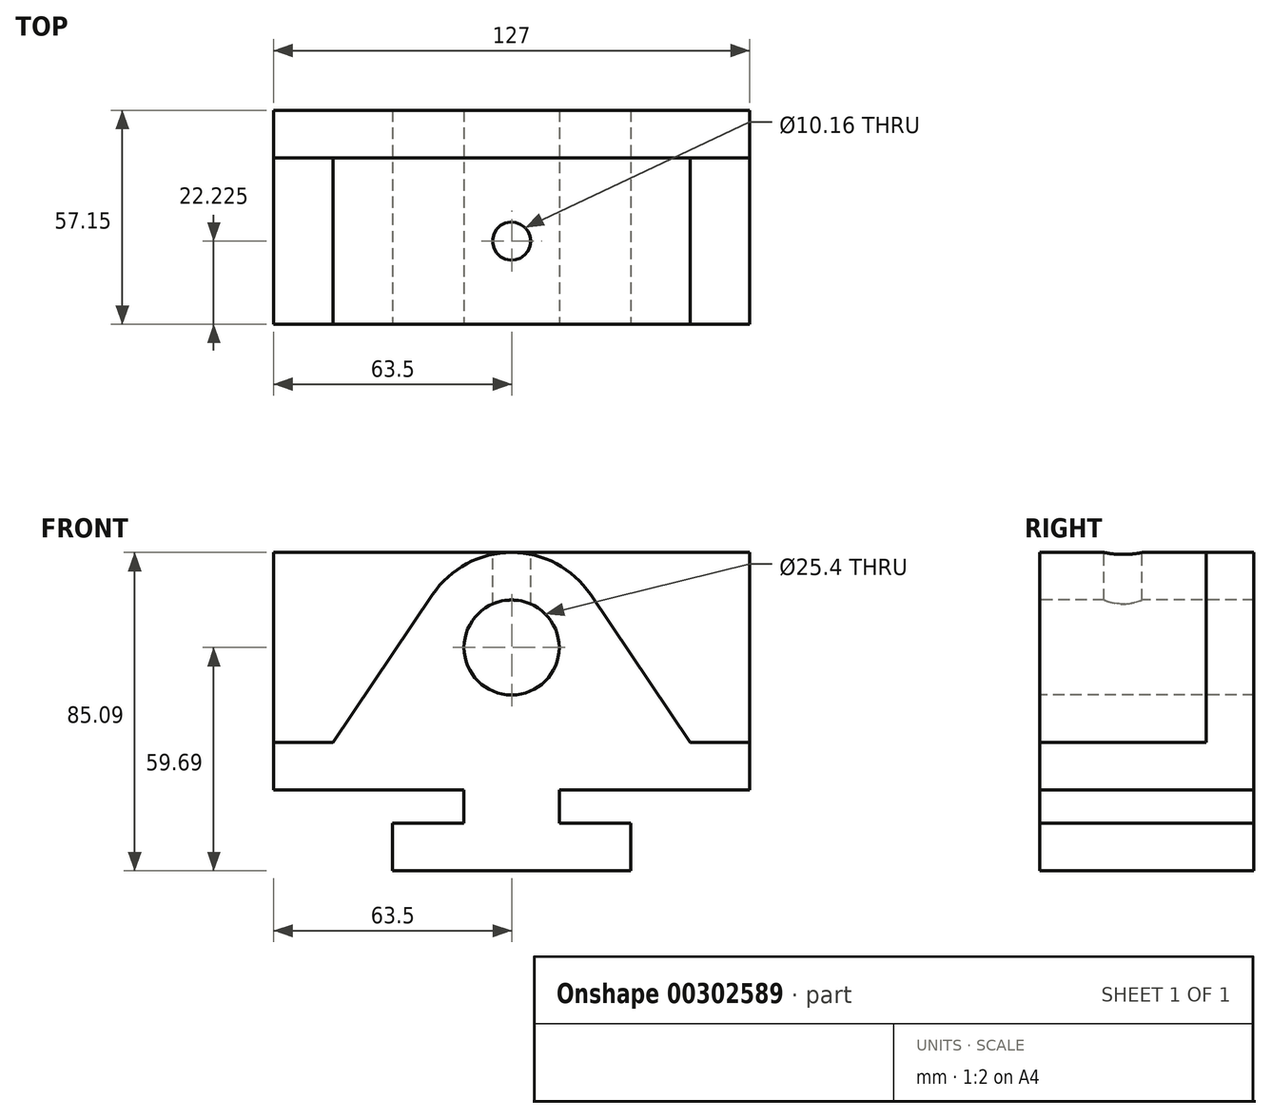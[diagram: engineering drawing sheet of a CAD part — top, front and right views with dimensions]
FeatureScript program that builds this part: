
annotation { "Feature Type Name" : "Feature", "Feature Type Description" : "" }
export const myFeature = defineFeature(function(context is Context, id is Id, definition is map)
    precondition{}
    {
        {
            var Q0;
            Q0=qCreatedBy(makeId("Front.planeOp"),FACE);
            var sketch = newSketch(context, id + "F0", { "sketchPlane" : qUnion([Q0])});
            skLineSegment(sketch, "E0.bottom", {"start": v(0, 0) * mm, "end": v(50.8, 0) * mm});
            skLineSegment(sketch, "E0.top", {"start": v(0, 63.5) * mm, "end": v(127, 63.5) * mm});
            skLineSegment(sketch, "E0.left", {"start": v(0, 0) * mm, "end": v(0, 63.5) * mm});
            skLineSegment(sketch, "E0.right", {"start": v(127, 0) * mm, "end": v(127, 63.5) * mm});
            skLineSegment(sketch, "E1", {"start": v(63.5, 64.06) * mm, "end": v(63.5, 0) * mm, "construction": true});
            skPoint(sketch, "E1.startSnap0", {"position": v(63.5, 63.5) * mm});
            skLineSegment(sketch, "E2", {"start": v(63.5, 0) * mm, "end": v(63.5, -46.89) * mm, "construction": true});
            skLineSegment(sketch, "E3", {"start": v(50.8, 0) * mm, "end": v(50.8, -8.89) * mm});
            skLineSegment(sketch, "E4", {"start": v(50.8, -8.89) * mm, "end": v(31.75, -8.9) * mm});
            skLineSegment(sketch, "E5", {"start": v(31.75, -8.9) * mm, "end": v(31.75, -21.6) * mm});
            skLineSegment(sketch, "E6", {"start": v(31.75, -21.59) * mm, "end": v(95.25, -21.59) * mm});
            skLineSegment(sketch, "E7", {"start": v(95.25, -21.6) * mm, "end": v(95.25, -8.89) * mm});
            skLineSegment(sketch, "E8", {"start": v(95.25, -8.89) * mm, "end": v(76.2, -8.89) * mm});
            skLineSegment(sketch, "E9", {"start": v(76.2, -8.89) * mm, "end": v(76.2, 0) * mm});
            skLineSegment(sketch, "E10.trimOffspring", {"start": v(76.2, 0) * mm, "end": v(127, 0) * mm});
            skLineSegment(sketch, "E11", {"start": v(0, 0) * mm, "end": v(0, 12.7) * mm});
            skLineSegment(sketch, "E12", {"start": v(0, 12.7) * mm, "end": v(15.87, 12.7) * mm});
            skLineSegment(sketch, "E13", {"start": v(15.87, 12.7) * mm, "end": v(42.4, 52.25) * mm});
            skLineSegment(sketch, "E14", {"start": v(84.6, 52.25) * mm, "end": v(111.13, 12.7) * mm});
            skLineSegment(sketch, "E15", {"start": v(111.12, 12.7) * mm, "end": v(127, 12.7) * mm});
            skLineSegment(sketch, "E16", {"start": v(127, 12.7) * mm, "end": v(127, 0) * mm});
            skArc(sketch, "E17", {"start": v(84.6, 52.25) * mm, "mid": v(63.5, 63.5) * mm, "end": v(42.4, 52.25) * mm});
            skCircle(sketch, "E18", {"center": v(63.5, 38.1) * mm, "radius": 12.7 * mm});
            skSolve(sketch);
        }
        {
            var Q0;
            Q0=makeQuery(id+"F0.imprint","IMPRINT",FACE,{"disambiguationData":[TD([[makeQuery(id+"F0.imprint","IMPRINT",EDGE,{"derivedFrom":sQuery(id+"F0.wireOp",EDGE,"E0.bottom")}),1.0]])]});
            var Q1;
            {var subQ1=sQuery(id+"F0.wireOp",EDGE,"E0.left");Q1=makeQuery(id+"F0.imprint","IMPRINT",FACE,{"disambiguationData":[TD([[makeQuery(id+"F0.imprint","IMPRINT",EDGE,{"derivedFrom":subQ1}),-1.0]])]});}
            var Q2;
            {var subQ1=sQuery(id+"F0.wireOp",EDGE,"E0.right");Q2=makeQuery(id+"F0.imprint","IMPRINT",FACE,{"disambiguationData":[TD([[makeQuery(id+"F0.imprint","IMPRINT",EDGE,{"derivedFrom":subQ1}),1.0]])]});}
            extrude(context, id + "F1", {"entities" : qUnion([Q0, Q1, Q2]), "oppositeDirection" : true, "depth" : 57.15 * mm});
        }
        {
            var Q0;
            {var subQ1=sQuery(id+"F0.wireOp",EDGE,"E0.right");Q0=makeQuery(id+"F0.imprint","IMPRINT",FACE,{"disambiguationData":[TD([[makeQuery(id+"F0.imprint","IMPRINT",EDGE,{"derivedFrom":subQ1}),1.0]])]});}
            var Q1;
            {var subQ1=sQuery(id+"F0.wireOp",EDGE,"E0.left");Q1=makeQuery(id+"F0.imprint","IMPRINT",FACE,{"disambiguationData":[TD([[makeQuery(id+"F0.imprint","IMPRINT",EDGE,{"derivedFrom":subQ1}),-1.0]])]});}
            extrude(context, id + "F2", {"entities" : qUnion([Q0, Q1]), "operationType" : NewBodyOperationType.REMOVE, "oppositeDirection" : true, "depth" : 44.45 * mm});
        }
        {
            var Q0;
            Q0=makeQuery(id+"F1.opExtrude","SWEPT_FACE",FACE,{"disambiguationData":[OSD([sQuery(id+"F0.wireOp",EDGE,"E0.top")])]});
            var sketch = newSketch(context, id + "F3", { "sketchPlane" : qUnion([Q0])});
            skLineSegment(sketch, "E19", {"start": v(84.6, 22.23) * mm, "end": v(42.4, 22.22) * mm, "construction": true});
            skLineSegment(sketch, "E20", {"start": v(63.5, 44.45) * mm, "end": v(63.5, 0) * mm, "construction": true});
            skCircle(sketch, "E21", {"center": v(63.5, 22.22) * mm, "radius": 5.08 * mm});
            skSolve(sketch);
        }
        {
            var Q0;
            Q0=makeQuery(id+"F3.imprint","IMPRINT",FACE,{"disambiguationData":[TD([[makeQuery(id+"F3.imprint","IMPRINT",EDGE,{"derivedFrom":sQuery(id+"F3.wireOp",EDGE,"E21")}),1.0]])]});
            extrude(context, id + "F4", {"entities" : qUnion([Q0]), "operationType" : NewBodyOperationType.REMOVE, "oppositeDirection" : true, "depth" : 25.4 * mm});
        }
    });
